# Revit family: Gewindeplatte 28x15
name_source: partatom
category: HLS-Bauteile
revit_build: Autodesk Revit 2017 (Build: 20190507_1515(x64)
units: mm (PartAtom-declared; Revit-internal decimal feet)

## family parameters
Arbeitsebenenbasiert = Ja
Beim Laden mit Abzugskörper schneiden = Nein
Bemaßung runder Anschluss = Durchmesser verwenden
Gemeinsam genutzt = Ja
Immer vertikal = Nein
Raumberechnungspunkt = Nein
Teiletyp = Normal

## types (1)
- Gewindeplatte 28x15 M 8
    Artikelnummer = 0750069
    Breite = 13 mm
    EAN = 4250928417121
    Fabrikat = MEFA
    Firma = MEFA Befestigungs- und Montagesysteme GmbH
    Gewicht = 0.01 kg
    Gewicht pro Bauteil = 0.01 kg
    Kurztext1 = Gewindeplatte
    Kurztext2 = M8 28x15 gvz
    Länge = 24 mm  [stored 0.0787402 ft]
    Material = Stahl
    Materialname = S235
    Mengeneinheit = St
    Oberflaeche = galvanisch verzinkt
    Profiltyp = 27
    Stärke = 0 mm  [stored 0 ft]
    Vorgabe-Ansicht = 1219 mm
    d2 = 4 mm  [stored 0.0131234 ft]
    vpe = 100 St

note: [stored X ft] marks values corroborated as IEEE doubles in the binary element streams (Revit-internal decimal feet)
